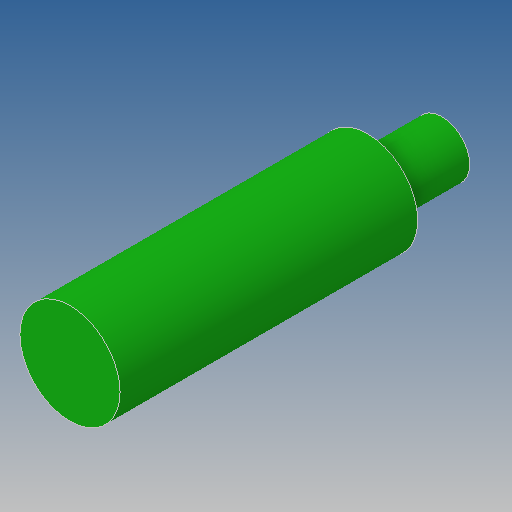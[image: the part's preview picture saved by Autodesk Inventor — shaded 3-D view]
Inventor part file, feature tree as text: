
AUTODESK INVENTOR PART (.ipt)
format: ipt  version: 2018 (Build 220112000, 112)  size: 101,376 bytes
history: native  units: mm
features: other x3, extrude x2, sketch x2, reference x1
ambient origin geometry x8: Origin, YZ Plane, XZ Plane, XY Plane, X Axis, Y Axis, Z Axis, Center Point
bodies: Solid1 (feature_tree)
feature tree (8):
  extrude  "Extrusion1"  Depth=80.0mm TaperAngle=0.0deg
  extrude  "Extrusion2"  [1 undecoded]
  sketch  "Sketch1"  dims[d0=20.0mm d1=0.0mm d2=80.0mm d3=0.0mm]
  reference  "Reference1"
  sketch  "Sketch2"
  other  "<userpath>\OneDrive\Objet3D\EPFLEplucheCarrote\Assembly1.iam"
  other  "Assembly1.iam"
  other  "Manivelle:1"
note: 1 required parameter value undecoded (feature->parameter linkage not recoverable at this tier; creation-order binding heuristic only, values carry confidence <= 0.55)
